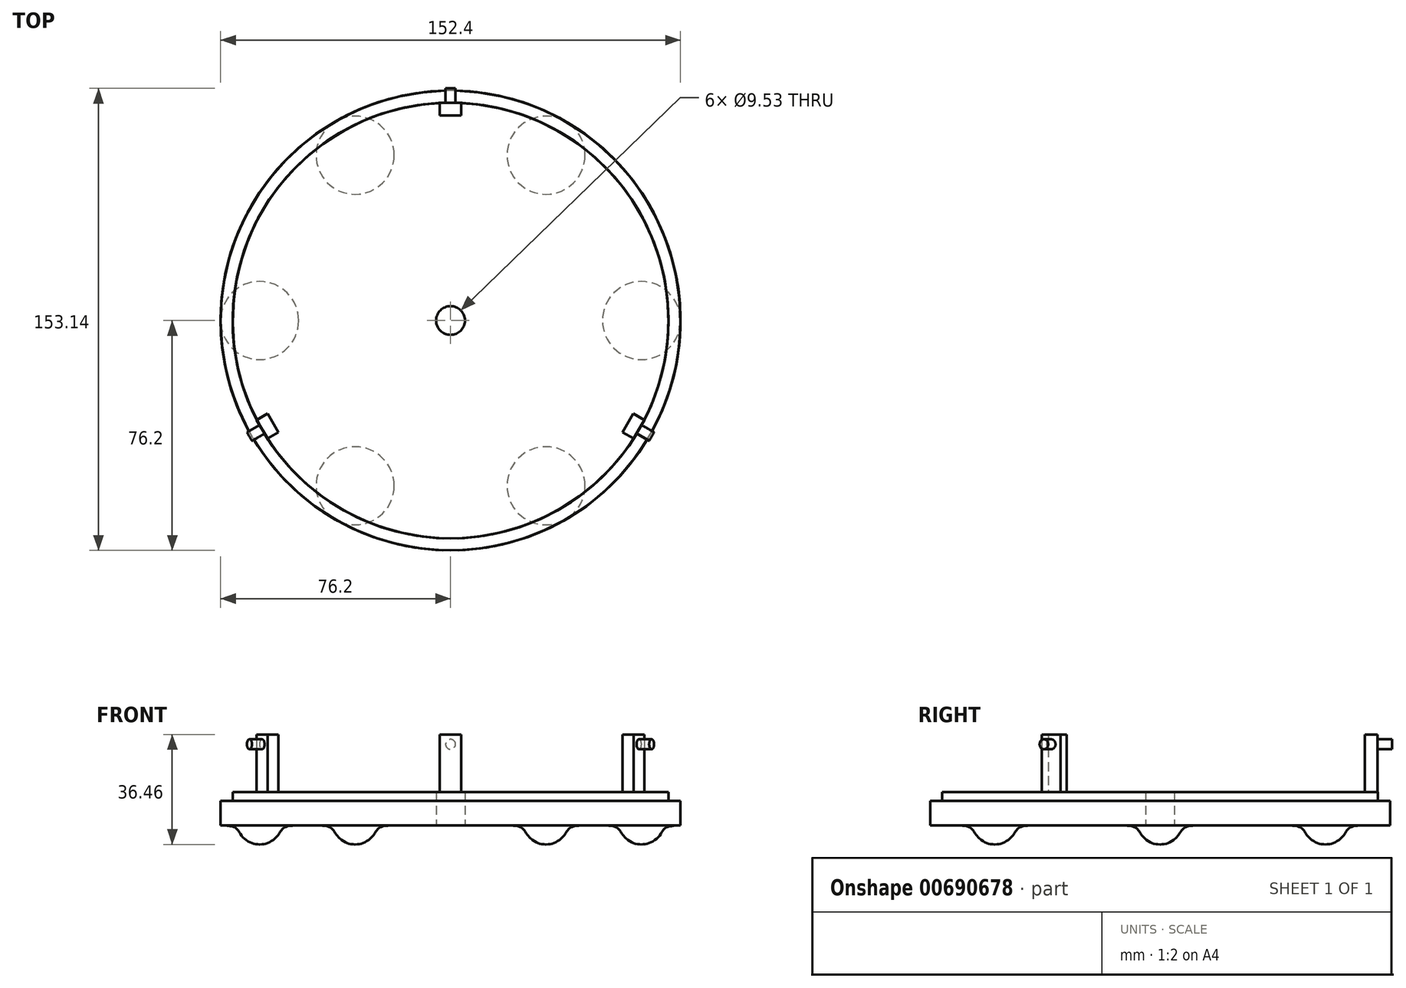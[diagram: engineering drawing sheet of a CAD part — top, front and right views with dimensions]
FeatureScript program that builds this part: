
annotation { "Feature Type Name" : "Feature", "Feature Type Description" : "" }
export const myFeature = defineFeature(function(context is Context, id is Id, definition is map)
    precondition{}
    {
        {
            var Q0;
            Q0=qCreatedBy(makeId("Front.planeOp"),FACE);
            var sketch = newSketch(context, id + "F0", { "sketchPlane" : qUnion([Q0])});
            skLineSegment(sketch, "E0", {"start": v(0, 0) * mm, "end": v(0, 67.93) * mm, "construction": true});
            skLineSegment(sketch, "E1.bottom", {"start": v(4.76, 0) * mm, "end": v(76.2, 0) * mm});
            skLineSegment(sketch, "E1.top", {"start": v(4.76, 8.03) * mm, "end": v(76.2, 8.03) * mm});
            skLineSegment(sketch, "E1.left", {"start": v(4.76, 0) * mm, "end": v(4.76, 8.03) * mm});
            skLineSegment(sketch, "E1.right", {"start": v(76.2, 0) * mm, "end": v(76.2, 8.03) * mm});
            skLineSegment(sketch, "E2.bottom", {"start": v(4.76, 8.03) * mm, "end": v(72.2, 8.03) * mm});
            skLineSegment(sketch, "E2.top", {"start": v(4.76, 11.06) * mm, "end": v(72.2, 11.06) * mm});
            skLineSegment(sketch, "E2.left", {"start": v(4.76, 8.03) * mm, "end": v(4.76, 11.06) * mm});
            skLineSegment(sketch, "E2.right", {"start": v(72.2, 8.03) * mm, "end": v(72.2, 11.06) * mm});
            skSolve(sketch);
        }
        {
            var Q0;
            Q0 = qSketchRegion(id + "F0", true);
            var Q1;
            Q1=sQuery(id+"F0.wireOp",EDGE,"E0");
            revolve(context, id + "F1", {"surfaceOperationType" : NewSurfaceOperationType.NEW, "entities" : qUnion([Q0]), "axis" : qUnion([Q1]), "revolveType" : RevolveType.FULL});
        }
        {
            var Q0;
            Q0=qCreatedBy(makeId("Front.planeOp"),FACE);
            var sketch = newSketch(context, id + "F2", { "sketchPlane" : qUnion([Q0])});
            skLineSegment(sketch, "E3.0", {"start": v(4.76, 0) * mm, "end": v(76.2, 0) * mm});
            skLineSegment(sketch, "E4", {"start": v(63.26, 0) * mm, "end": v(63.26, -6.35) * mm});
            skPoint(sketch, "E5.visualSharp", {"position": v(72.43, -6.35) * mm});
            skFitSpline(sketch, "E6", {"points": [v(63.26, -6.35) * mm, v(66.1, -5.82) * mm, v(69.13, -3.6) * mm, v(70.63, -1.4) * mm, v(72.45, -0.38) * mm, v(76.2, 0) * mm], "startDerivative": vector(15.22, 0.2) * mm, "endDerivative": vector(18, 1.46) * mm});
            skSolve(sketch);
        }
        {
            var Q0;
            Q0 = qSketchRegion(id + "F2", true);
            var Q1;
            Q1=sQuery(id+"F2.wireOp",EDGE,"E4");
            revolve(context, id + "F3", {"surfaceOperationType" : NewSurfaceOperationType.NEW, "entities" : qUnion([Q0]), "axis" : qUnion([Q1]), "revolveType" : RevolveType.FULL});
        }
        {
            var Q0;
            Q0=makeQuery(id+"F3.opRevolve","SWEPT_BODY",BODY,{"disambiguationData":[OSD([sQuery(id+"F2.wireOp",EDGE,"E3.0"),sQuery(id+"F2.wireOp",EDGE,"AbcQK6E3-c3Tc-PTnA-sdeN-6MsBevEzGBzT"),sQuery(id+"F2.wireOp",EDGE,"E4")])]});
            var Q1;
            Q1=makeQuery(id+"F1.opRevolve","SWEPT_BODY",BODY,{"disambiguationData":[OSD([sQuery(id+"F0.wireOp",EDGE,"E1.bottom"),sQuery(id+"F0.wireOp",EDGE,"E1.top"),sQuery(id+"F0.wireOp",EDGE,"E1.left"),sQuery(id+"F0.wireOp",EDGE,"E1.right"),sQuery(id+"F0.wireOp",EDGE,"E2.top"),sQuery(id+"F0.wireOp",EDGE,"E2.left"),sQuery(id+"F0.wireOp",EDGE,"E2.right")])]});
            var Q2;
            Q2=sQuery(id+"F0.wireOp",EDGE,"E0");
            circularPattern(context, id + "F4", {"entities" : qUnion([Q0, Q1]), "axis" : qUnion([Q2]), "angle" : 360 * degree, "instanceCount" : 6, "equalSpace" : true});
        }
        {
            var Q0;
            Q0=makeQuery(id+"F4.opPattern","COPY",FACE,{"derivedFrom":makeQuery(id+"F1.opRevolve","SWEPT_FACE",FACE,{"disambiguationData":[OSD([sQuery(id+"F0.wireOp",EDGE,"E2.top")])]}),"instanceName":"1"});
            var sketch = newSketch(context, id + "F5", { "sketchPlane" : qUnion([Q0])});
            skLineSegment(sketch, "E7", {"start": v(0, 0) * mm, "end": v(72.2, 0) * mm, "construction": true});
            skLineSegment(sketch, "E8", {"start": v(72.2, 0) * mm, "end": v(0, 0) * mm, "construction": true});
            skLineSegment(sketch, "E9", {"start": v(0, 0) * mm, "end": v(62.53, -36.1) * mm, "construction": true});
            skLineSegment(sketch, "E10", {"start": v(60.68, -39.14) * mm, "end": v(57.04, -37.05) * mm});
            skLineSegment(sketch, "E11", {"start": v(57.04, -37.05) * mm, "end": v(58.82, -33.96) * mm});
            skLineSegment(sketch, "E12.MirrorCS", {"start": v(60.6, -30.88) * mm, "end": v(58.82, -33.96) * mm});
            skLineSegment(sketch, "E13.MirrorCS", {"start": v(64.24, -32.98) * mm, "end": v(60.6, -30.88) * mm});
            skCircle(sketch, "E14.0", {"center": v(0, 0) * mm, "radius": 72.2 * mm});
            skLineSegment(sketch, "E15", {"start": v(64.24, -32.98) * mm, "end": v(60.68, -39.14) * mm});
            skSolve(sketch);
        }
        {
            var Q0;
            {var subQ1=sQuery(id+"F5.wireOp",EDGE,"E10");Q0=makeQuery(id+"F5.imprint","IMPRINT",FACE,{"disambiguationData":[TD([[makeQuery(id+"F5.imprint","IMPRINT",EDGE,{"derivedFrom":subQ1}),-1.0]])]});}
            extrude(context, id + "F6", {"entities" : qUnion([Q0]), "depth" : 19.05 * mm, "offsetDistance" : 25.4 * mm});
        }
        {
            var Q0;
            Q0=makeQuery(id+"F6.opExtrude","SWEPT_FACE",FACE,{"disambiguationData":[OSD([sQuery(id+"F5.wireOp",EDGE,"E15")])]});
            var sketch = newSketch(context, id + "F7", { "sketchPlane" : qUnion([Q0])});
            skLineSegment(sketch, "E16", {"start": v(0, 30.11) * mm, "end": v(0, 11.06) * mm, "construction": true});
            skCircle(sketch, "E17", {"center": v(0, 26.84) * mm, "radius": 1.65 * mm});
            skSolve(sketch);
        }
        {
            var Q0;
            Q0 = qSketchRegion(id + "F7", true);
            extrude(context, id + "F8", {"entities" : qUnion([Q0]), "operationType" : NewBodyOperationType.ADD, "depth" : 4.83 * mm, "offsetDistance" : 25.4 * mm});
        }
        {
            var Q0;
            Q0=makeQuery(id+"F6.opExtrude","SWEPT_BODY",BODY,{"disambiguationData":[OSD([sQuery(id+"F5.wireOp",EDGE,"E10"),sQuery(id+"F5.wireOp",EDGE,"E11"),sQuery(id+"F5.wireOp",EDGE,"E12.MirrorCS"),sQuery(id+"F5.wireOp",EDGE,"E13.MirrorCS"),sQuery(id+"F5.wireOp",EDGE,"E14.0")])]});
            var Q1;
            Q1=sQuery(id+"F0.wireOp",EDGE,"E0");
            circularPattern(context, id + "F9", {"entities" : qUnion([Q0]), "axis" : qUnion([Q1]), "angle" : 360 * degree, "instanceCount" : 3, "equalSpace" : true});
        }
    });
